# Revit family: Boiler-Commercial_Remeha_P420
name_source: partatom
category: Mechanical Equipment
revit_build: Autodesk Revit MEP 2012 (Build: 20110309_2315(x64)
units: mm (PartAtom-declared; Revit-internal decimal feet)

## types (7) — shared parameters
Assembly Code = D3020100
Black = Black
Blue = BLue
Boiler Height incl top control panel - mm = 1690 mm
Boiler Width - mm = 1000 mm  [stored 3.28084 ft]
Clearance box required = Yes
Dark Blue = Dark Blue
DarkGrey = Dark Grey
Description = P Series Cast Iron Boilers
Drain Outlet = 50 mm  [stored 0.164042 ft]
Drain Outlet Radius = 25 mm  [stored 0.082021 ft]
Flue Gas temperature = <220
Front Clearance minimum  Note = NOTE: Adapt this dimension on the basis of the dimensions of the burner.
Fuse Rating to control panel = 10 Amp
Glass = Glass
Green = Green
High Limit Thermostat deg C = 110
Host Condition = Floor Standing
Installation URL = http://www.remeha.co.uk
Light Grey = Light Grey
Manufacturer = Remeha Commercial
Manufacturer Fax = 0118 978 6977
Maximum operating pressure -  Bar = 6
Product Page URL = http://www.remeha.co.uk
Rear Clearance = 1000 mm  [stored 3.28084 ft]
Red = Red
Sales Brochure = http://remeha.co.uk
Side Clearance Mininum = 500 mm
Side Clearance door opening side = 500 mm
Side Clearance door opening side Note = NOTE: Adapt this dimension on the basis of the dimensions of the burner.
Standard Operating Temperatures deg C = 30 - 90
Subcategory = Cast Iron Boilers
Technical Information URL = http://www.remeha.co.uk
URL = http://www.remeha.co.uk
Voltage to control panel = 230 -1 - 50
zero-valued in all types: Top Clearance above case minimum

## per-type parameters (varying)
| type | Boiler Length - Excluding Burner - mm | Dry Weight Kg | Flow Connection | Flow Connection Diameter | Flow Connection Radius | Flue Connection | Flue Connection Radius | Front Clearance Minimum | Hydraulic resistance at 10 dT - mbar | Hydraulic resistance at 20dT -  mbar | Mass flue gas flow  Gas Kg/h | Mass flue gas flow Fuel oil Kg/hr | Nominal flow rate at 20dT | Number of sections | Rated output kW | Return Connection | Return Connection Diameter | Return Connection Radius | Water content litres |
| P420 - 14 | 2785 mm | 2550 | 76 mm | 76 mm | 38 mm | 300 mm | 150 mm | 2500 mm | 194 | 49 | 1405 | 1450 | 9.32 | 14 | 780 | 76 mm | 76 mm | 38 mm | 624 |
| P420 - 13 | 2625 mm | 2370 | 76 mm | 76 mm | 38 mm | 300 mm | 150 mm | 2500 mm | 158 | 40 | 1297 | 1200 | 8.6 | 13 | 720 | 76 mm | 76 mm | 38 mm | 581 |
| P420 - 10 | 2120 mm | 1830 | 64 mm | 64 mm | 32 mm | 250 mm  [stored 0.82021 ft] | 125 mm  [stored 0.410105 ft] | 2000 mm  [stored 6.56168 ft] | 80 | 20 | 972 | 900 | 6.45 | 10 | 540 | 64 mm | 64 mm | 32 mm | 452 |
| P420 - 12 | 2465 mm | 2190 | 76 mm | 76 mm | 38 mm | 300 mm | 150 mm | 2500 mm | 130 | 33 | 1207 | 1116 | 8.00 | 12 | 670 | 76 mm | 76 mm | 38 mm | 538 |
| P420 - 11 | 2305 mm | 2010 | 76 mm | 76 mm | 38 mm | 300 mm | 150 mm | 2000 mm  [stored 6.56168 ft] | 101 | 25 | 1080 | 1000 | 7.17 | 11 | 600 | 76 mm | 76 mm | 38 mm | 495 |
| P420 - 9 | 1950 mm | 1650 | 64 mm | 64 mm | 32 mm | 250 mm  [stored 0.82021 ft] | 125 mm  [stored 0.410105 ft] | 2000 mm  [stored 6.56168 ft] | 48 | 12 | 810 | 750 | 5.38 | 9 | 450 | 64 mm | 64 mm | 32 mm | 409 |
| P420 - 8 | 1800 mm  [stored 5.90551 ft] | 1470 | 64 mm | 64 mm | 32 mm | 250 mm  [stored 0.82021 ft] | 125 mm  [stored 0.410105 ft] | 1500 mm  [stored 4.92126 ft] | 31 | 8 | 700 | 650 | 4.66 | 8 | 390 | 64 mm | 64 mm | 32 mm | 366 |

note: column(s) folded — value = type name in every type: Model

note: [stored X ft] marks values corroborated as IEEE doubles in the binary element streams (Revit-internal decimal feet)

## geometry (parser evidence)
native form markers: Sweep x3
no freeform markers — native parametric forms only
